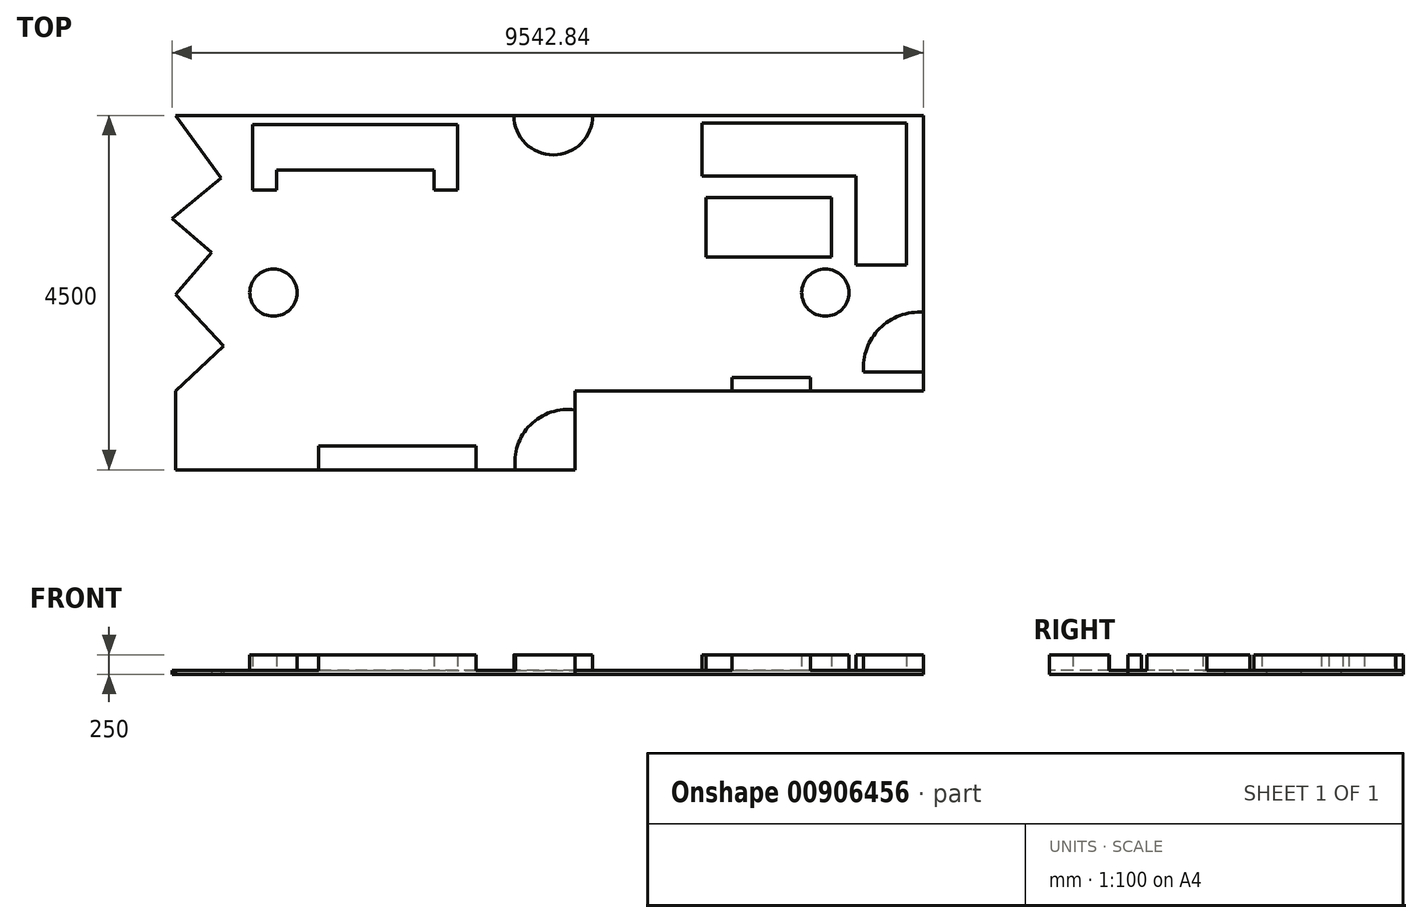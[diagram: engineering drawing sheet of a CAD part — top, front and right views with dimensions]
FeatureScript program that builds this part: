
annotation { "Feature Type Name" : "Feature", "Feature Type Description" : "" }
export const myFeature = defineFeature(function(context is Context, id is Id, definition is map)
    precondition{}
    {
        {
            var Q0;
            Q0=qCreatedBy(makeId("Top.planeOp"),FACE);
            var sketch = newSketch(context, id + "F0", { "sketchPlane" : qUnion([Q0])});
            skLineSegment(sketch, "E0", {"start": v(-5077.09, 2275.5) * mm, "end": v(-777.09, 2275.5) * mm});
            skLineSegment(sketch, "E1", {"start": v(-777.09, 2275.5) * mm, "end": v(222.91, 2275.5) * mm});
            skLineSegment(sketch, "E2", {"start": v(222.91, 2275.5) * mm, "end": v(4422.91, 2275.5) * mm});
            skLineSegment(sketch, "E3", {"start": v(4422.91, 2275.5) * mm, "end": v(4422.91, -1224.5) * mm});
            skLineSegment(sketch, "E4", {"start": v(-5077.09, 2275.5) * mm, "end": v(-4499.2, 1480.78) * mm});
            skLineSegment(sketch, "E5", {"start": v(-4499.2, 1480.78) * mm, "end": v(-5119.93, 968.86) * mm});
            skLineSegment(sketch, "E6", {"start": v(-5119.93, 968.86) * mm, "end": v(-4616.29, 535.39) * mm});
            skLineSegment(sketch, "E7", {"start": v(-4616.29, 535.39) * mm, "end": v(-5077.09, 0) * mm});
            skLineSegment(sketch, "E8", {"start": v(-5077.09, 0) * mm, "end": v(-4466.1, -651.54) * mm});
            skLineSegment(sketch, "E9", {"start": v(-4466.1, -651.54) * mm, "end": v(-5077.09, -1224.5) * mm});
            skLineSegment(sketch, "E10", {"start": v(4422.91, -1224.5) * mm, "end": v(-5077.09, -1224.5) * mm});
            skLineSegment(sketch, "E11", {"start": v(0, -1224.5) * mm, "end": v(0, -2224.5) * mm});
            skLineSegment(sketch, "E12", {"start": v(-5077.09, -1224.5) * mm, "end": v(-5077.09, -2224.5) * mm});
            skLineSegment(sketch, "E13", {"start": v(-5077.09, -2224.5) * mm, "end": v(0, -2224.5) * mm});
            skSolve(sketch);
        }
        {
            var Q0;
            Q0 = qSketchRegion(id + "F0", true);
            extrude(context, id + "F1", {"entities" : qUnion([Q0]), "depth" : 50 * mm, "offsetDistance" : 25 * mm});
        }
        {
            var Q0;
            Q0=makeQuery(id+"F1.opExtrude","CAP_FACE",FACE,{"disambiguationData":[OSD([sQuery(id+"F0.wireOp",EDGE,"E0"),sQuery(id+"F0.wireOp",EDGE,"E1"),sQuery(id+"F0.wireOp",EDGE,"E2"),sQuery(id+"F0.wireOp",EDGE,"E3"),sQuery(id+"F0.wireOp",EDGE,"JsJC2qk8-IMfp-q7EB-e2qi-tZzDDmBO7Eud"),sQuery(id+"F0.wireOp",EDGE,"uyk6A429-sQxN-8OGI-89aS-fQe6hI1wWgI8"),sQuery(id+"F0.wireOp",EDGE,"FhDqHBpY-2mV3-Oogz-ZoIL-EUJ2pRtQZvll"),sQuery(id+"F0.wireOp",EDGE,"od4UTXKM-8ZmB-3kie-6vXC-qKuINCIEBg7y"),sQuery(id+"F0.wireOp",EDGE,"E4"),sQuery(id+"F0.wireOp",EDGE,"E5"),sQuery(id+"F0.wireOp",EDGE,"E6"),sQuery(id+"F0.wireOp",EDGE,"E7"),sQuery(id+"F0.wireOp",EDGE,"E8"),sQuery(id+"F0.wireOp",EDGE,"E9"),sQuery(id+"F0.wireOp",EDGE,"EEWjQB9i-ifuF-boS6-3JjP-pwuFpdgnBD6Y"),sQuery(id+"F0.wireOp",EDGE,"6HCbGPT6-XH75-kz8J-TDNR-8NLORYTXgddJ")])],"isStart":false});
            var sketch = newSketch(context, id + "F2", { "sketchPlane" : qUnion([Q0])});
            skLineSegment(sketch, "E14.bottom", {"start": v(-4094.82, 2159.77) * mm, "end": v(-1494.82, 2159.77) * mm});
            skLineSegment(sketch, "E14.top", {"start": v(-4094.82, 1579.77) * mm, "end": v(-1494.82, 1579.77) * mm});
            skLineSegment(sketch, "E14.left", {"start": v(-4094.82, 2159.77) * mm, "end": v(-4094.82, 1579.77) * mm});
            skLineSegment(sketch, "E14.right", {"start": v(-1494.82, 2159.77) * mm, "end": v(-1494.82, 1579.77) * mm});
            skLineSegment(sketch, "E15", {"start": v(1609.4, 2177.07) * mm, "end": v(4209.4, 2177.07) * mm});
            skLineSegment(sketch, "E16", {"start": v(4209.4, 2177.07) * mm, "end": v(4209.4, 377.07) * mm});
            skLineSegment(sketch, "E17", {"start": v(4209.4, 377.07) * mm, "end": v(3566.82, 377.07) * mm});
            skLineSegment(sketch, "E18", {"start": v(3566.82, 377.07) * mm, "end": v(3566.82, 1507.42) * mm});
            skLineSegment(sketch, "E19", {"start": v(3566.82, 1507.42) * mm, "end": v(1609.4, 1507.42) * mm});
            skLineSegment(sketch, "E20", {"start": v(1609.4, 1507.42) * mm, "end": v(1609.4, 2177.07) * mm});
            skLineSegment(sketch, "E21.bottom", {"start": v(1660.9, 1232.7) * mm, "end": v(3257.76, 1232.7) * mm});
            skLineSegment(sketch, "E21.top", {"start": v(1660.9, 477.2) * mm, "end": v(3257.76, 477.2) * mm});
            skLineSegment(sketch, "E21.left", {"start": v(1660.9, 1232.7) * mm, "end": v(1660.9, 477.2) * mm});
            skLineSegment(sketch, "E21.right", {"start": v(3257.76, 1232.7) * mm, "end": v(3257.76, 477.2) * mm});
            skLineSegment(sketch, "E22.bottom", {"start": v(1992.2, -1224.5) * mm, "end": v(2992.2, -1224.5) * mm});
            skLineSegment(sketch, "E22.top", {"start": v(1992.2, -1052.4) * mm, "end": v(2992.2, -1052.4) * mm});
            skLineSegment(sketch, "E22.left", {"start": v(1992.2, -1224.5) * mm, "end": v(1992.2, -1052.4) * mm});
            skLineSegment(sketch, "E22.right", {"start": v(2992.2, -1224.5) * mm, "end": v(2992.2, -1052.4) * mm});
            skArc(sketch, "E23", {"start": v(-777.09, 2275.5) * mm, "mid": v(-277.09, 1775.5) * mm, "end": v(222.91, 2275.5) * mm});
            skLineSegment(sketch, "E24", {"start": v(-777.09, 2275.5) * mm, "end": v(222.91, 2275.5) * mm});
            skLineSegment(sketch, "E25", {"start": v(4422.91, -984.12) * mm, "end": v(3662.91, -984.12) * mm});
            skLineSegment(sketch, "E26", {"start": v(4422.91, -984.12) * mm, "end": v(4422.91, -224.12) * mm});
            skArc(sketch, "E27", {"start": v(4422.91, -224.12) * mm, "mid": v(3868.77, -429.98) * mm, "end": v(3662.91, -984.12) * mm});
            skPoint(sketch, "E28", {"position": v(4422.91, -984.12) * mm});
            skPoint(sketch, "E29", {"position": v(2992.2, -1224.5) * mm});
            skLineSegment(sketch, "E30.top", {"start": v(1742.2, -624.5) * mm, "end": v(3242.2, -624.5) * mm});
            skLineSegment(sketch, "E30.left", {"start": v(1742.2, -1224.5) * mm, "end": v(1742.2, -624.5) * mm});
            skLineSegment(sketch, "E30.right", {"start": v(3242.2, -1045.6) * mm, "end": v(3242.2, -624.5) * mm});
            skLineSegment(sketch, "E31", {"start": v(-3260, -2224.5) * mm, "end": v(-1260, -2224.5) * mm});
            skLineSegment(sketch, "E32", {"start": v(-1260, -2224.5) * mm, "end": v(-1260, -1924.5) * mm});
            skLineSegment(sketch, "E33", {"start": v(-1260, -1924.5) * mm, "end": v(-3260, -1924.5) * mm});
            skLineSegment(sketch, "E34", {"start": v(-3260, -1924.5) * mm, "end": v(-3260, -2224.5) * mm});
            skLineSegment(sketch, "E35", {"start": v(0, -2224.5) * mm, "end": v(-760, -2224.5) * mm});
            skLineSegment(sketch, "E36", {"start": v(0, -2224.5) * mm, "end": v(0, -1464.5) * mm});
            skArc(sketch, "E37", {"start": v(0, -1464.5) * mm, "mid": v(-569.14, -1655.36) * mm, "end": v(-760, -2224.5) * mm});
            skLineSegment(sketch, "E38", {"start": v(-4094.82, 1579.77) * mm, "end": v(-4094.82, 1329.77) * mm});
            skLineSegment(sketch, "E39", {"start": v(-4094.82, 1329.77) * mm, "end": v(-3794.82, 1329.77) * mm});
            skLineSegment(sketch, "E40", {"start": v(-3794.82, 1329.77) * mm, "end": v(-3794.82, 1579.77) * mm});
            skLineSegment(sketch, "E41", {"start": v(-1494.82, 1579.77) * mm, "end": v(-1494.82, 1329.77) * mm});
            skLineSegment(sketch, "E42", {"start": v(-1494.82, 1329.77) * mm, "end": v(-1794.82, 1329.77) * mm});
            skLineSegment(sketch, "E43", {"start": v(-1794.82, 1329.77) * mm, "end": v(-1794.82, 1579.77) * mm});
            skLineSegment(sketch, "E44", {"start": v(-5077.09, 2275.5) * mm, "end": v(-327.09, 2275.5) * mm, "construction": true});
            skLineSegment(sketch, "E45", {"start": v(-327.09, 2275.5) * mm, "end": v(-327.09, -2224.5) * mm, "construction": true});
            skLineSegment(sketch, "E46", {"start": v(-327.09, 25.5) * mm, "end": v(-3832.09, 25.5) * mm, "construction": true});
            skLineSegment(sketch, "E47", {"start": v(-327.09, 25.5) * mm, "end": v(3177.91, 25.5) * mm, "construction": true});
            skCircle(sketch, "E48", {"center": v(-3832.09, 25.5) * mm, "radius": 300 * mm});
            skCircle(sketch, "E49", {"center": v(3177.91, 25.5) * mm, "radius": 300 * mm});
            skSolve(sketch);
        }
        {
            var Q0;
            Q0 = qSketchRegion(id + "F2", true);
            extrude(context, id + "F3", {"entities" : qUnion([Q0]), "operationType" : NewBodyOperationType.ADD, "depth" : 200 * mm, "offsetDistance" : 25 * mm});
        }
        {
            var Q0;
            Q0 = qSketchRegion(id + "F2", true);
            extrude(context, id + "F4", {"entities" : qUnion([Q0]), "operationType" : NewBodyOperationType.ADD, "depth" : 200 * mm, "offsetDistance" : 25 * mm});
        }
        {
            var Q0;
            Q0 = qSketchRegion(id + "F2", true);
            extrude(context, id + "F5", {"entities" : qUnion([Q0]), "operationType" : NewBodyOperationType.ADD, "depth" : 200 * mm, "offsetDistance" : 25 * mm});
        }
        {
            var Q0;
            Q0 = qSketchRegion(id + "F2", true);
            extrude(context, id + "F6", {"entities" : qUnion([Q0]), "operationType" : NewBodyOperationType.ADD, "depth" : 200 * mm, "offsetDistance" : 25 * mm});
        }
        {
            var Q0;
            Q0 = qSketchRegion(id + "F2", true);
            extrude(context, id + "F7", {"entities" : qUnion([Q0]), "operationType" : NewBodyOperationType.ADD, "depth" : 200 * mm, "offsetDistance" : 25 * mm});
        }
        {
            var Q0;
            Q0 = qSketchRegion(id + "F2", true);
            extrude(context, id + "F8", {"entities" : qUnion([Q0]), "operationType" : NewBodyOperationType.ADD, "depth" : 200 * mm, "offsetDistance" : 25 * mm});
        }
        {
            var Q0;
            Q0=sQuery(id+"F2.wireOp",EDGE,"E22.bottom");
            var Q1;
            Q1=sQuery(id+"F2.wireOp",EDGE,"E22.left");
            var Q2;
            Q2=sQuery(id+"F2.wireOp",EDGE,"E22.top");
            var Q3;
            Q3=sQuery(id+"F2.wireOp",EDGE,"E22.right");
            extrude(context, id + "F9", {"bodyType" : ToolBodyType.SURFACE, "surfaceEntities" : qUnion([Q0, Q1, Q2, Q3]), "depth" : 200 * mm, "offsetDistance" : 25 * mm});
        }
        {
            var Q0;
            Q0 = qSketchRegion(id + "F2", true);
            extrude(context, id + "F10", {"entities" : qUnion([Q0]), "operationType" : NewBodyOperationType.ADD, "depth" : 25 * mm, "offsetDistance" : 25 * mm});
        }
    });
